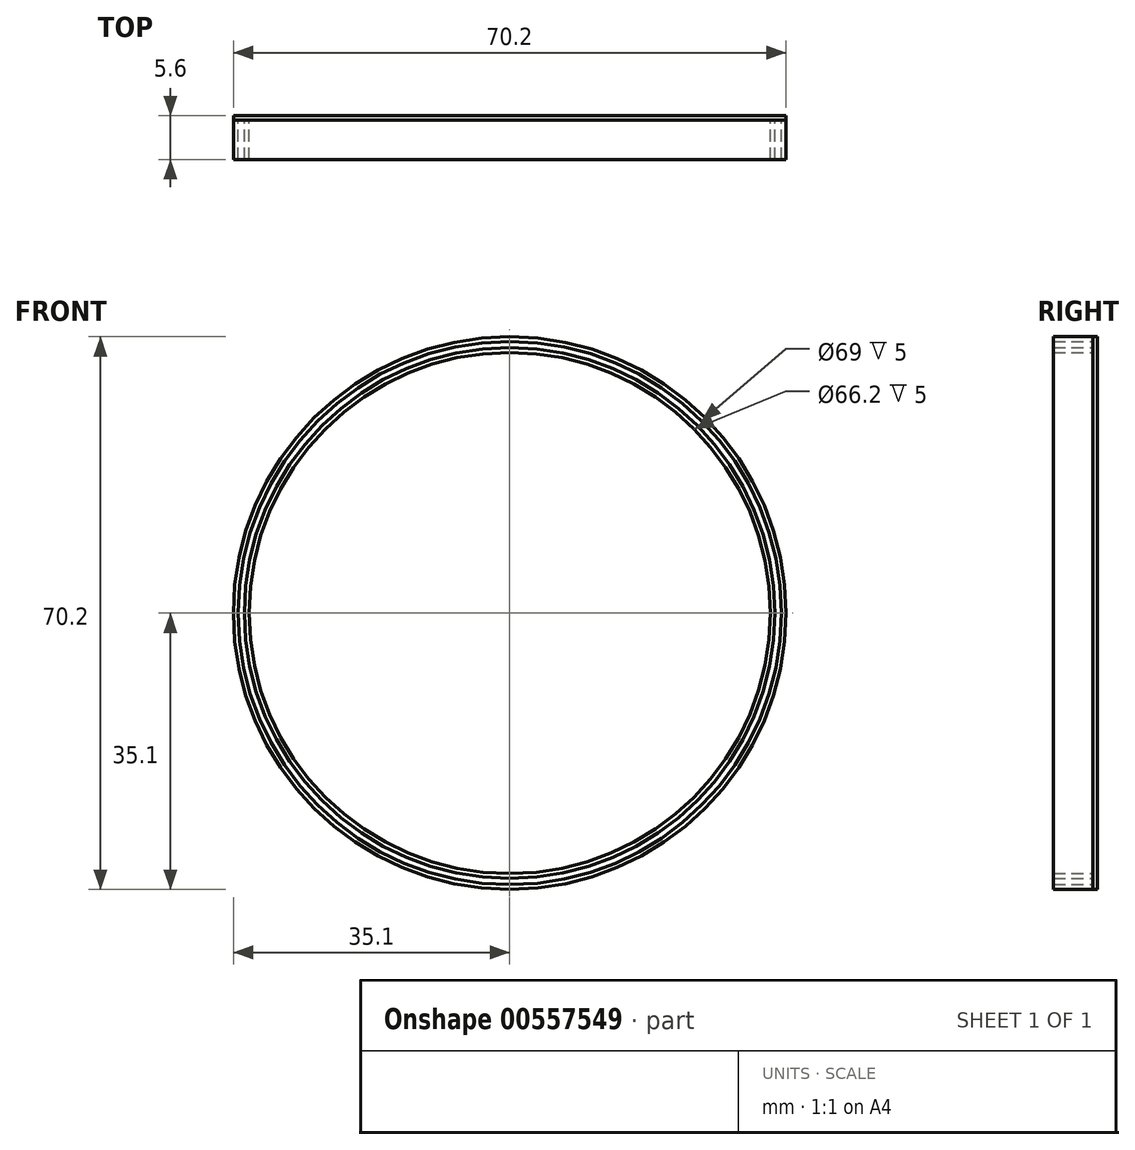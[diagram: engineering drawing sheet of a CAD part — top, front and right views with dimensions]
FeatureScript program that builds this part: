
annotation { "Feature Type Name" : "Feature", "Feature Type Description" : "" }
export const myFeature = defineFeature(function(context is Context, id is Id, definition is map)
    precondition{}
    {
        {
            var Q0;
            Q0=qCreatedBy(makeId("Front.planeOp"),FACE);
            var sketch = newSketch(context, id + "F0", { "sketchPlane" : qUnion([Q0])});
            skCircle(sketch, "E0", {"center": v(0, 0) * mm, "radius": 34.5 * mm});
            skCircle(sketch, "E1.0", {"center": v(0, 0) * mm, "radius": 35.1 * mm});
            skCircle(sketch, "E2.0", {"center": v(0, 0) * mm, "radius": 33.7 * mm});
            skCircle(sketch, "E3.0", {"center": v(0, 0) * mm, "radius": 33.1 * mm});
            skSolve(sketch);
        }
        {
            var Q0;
            Q0=makeQuery(id+"F0.imprint","IMPRINT",FACE,{"disambiguationData":[TD([[makeQuery(id+"F0.imprint","IMPRINT",EDGE,{"derivedFrom":sQuery(id+"F0.wireOp",EDGE,"E0")}),-1.0]])]});
            var Q1;
            Q1=makeQuery(id+"F0.imprint","IMPRINT",FACE,{"disambiguationData":[TD([[makeQuery(id+"F0.imprint","IMPRINT",EDGE,{"derivedFrom":sQuery(id+"F0.wireOp",EDGE,"E2.0")}),1.0]])]});
            extrude(context, id + "F1", {"entities" : qUnion([Q0, Q1]), "depth" : 5 * mm, "offsetDistance" : 25 * mm});
        }
        {
            var Q0;
            Q0=makeQuery(id+"F0.imprint","IMPRINT",FACE,{"disambiguationData":[TD([[makeQuery(id+"F0.imprint","IMPRINT",EDGE,{"derivedFrom":sQuery(id+"F0.wireOp",EDGE,"E0")}),-1.0]])]});
            var Q1;
            Q1=makeQuery(id+"F0.imprint","IMPRINT",FACE,{"disambiguationData":[TD([[makeQuery(id+"F0.imprint","IMPRINT",EDGE,{"derivedFrom":sQuery(id+"F0.wireOp",EDGE,"E0")}),1.0]])]});
            var Q2;
            Q2=makeQuery(id+"F0.imprint","IMPRINT",FACE,{"disambiguationData":[TD([[makeQuery(id+"F0.imprint","IMPRINT",EDGE,{"derivedFrom":sQuery(id+"F0.wireOp",EDGE,"E2.0")}),1.0]])]});
            var Q3;
            Q3=makeQuery(id+"F0.imprint","IMPRINT",FACE,{"disambiguationData":[TD([[makeQuery(id+"F0.imprint","IMPRINT",EDGE,{"derivedFrom":sQuery(id+"F0.wireOp",EDGE,"E3.0")}),1.0]])]});
            extrude(context, id + "F2", {"entities" : qUnion([Q0, Q1, Q2, Q3]), "oppositeDirection" : true, "depth" : 0.6 * mm, "offsetDistance" : 25 * mm});
        }
    });
